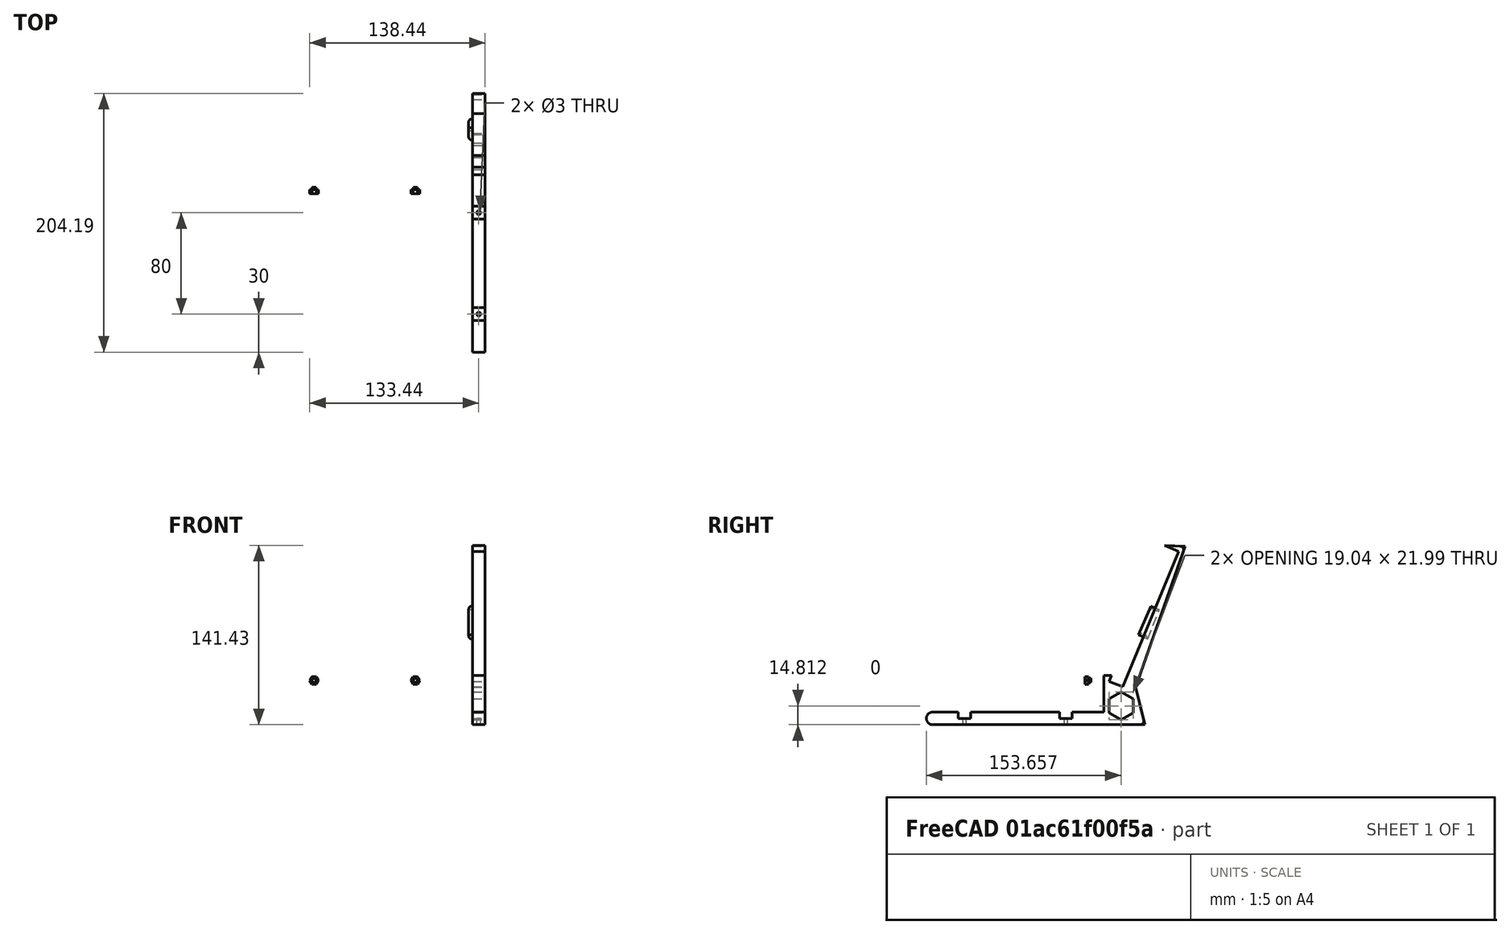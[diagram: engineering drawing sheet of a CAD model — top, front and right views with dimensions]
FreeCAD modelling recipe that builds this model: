
FCSTD DOCUMENT  (FreeCAD 0.16R6704 (Git))
Label: SOPORTE_LATERAL
License: All rights reserved
LicenseURL: http://en.wikipedia.org/wiki/All_rights_reserved
objects: Sketcher::SketchObject×4, PartDesign::Fillet×3, Mesh::Feature×2, PartDesign::Pad×2, PartDesign::Pocket×2
note: 15 computed .brp shape members not serialized (recipe doc carries the construction recipe); baked Part::Feature solids carry a one-line shape summary decoded from their .brp

FEATURE [Mesh::Feature] surround
  Placement = pos=(0,0,0) rot=(1,0,0;1.18682rad)
FEATURE [Sketcher::SketchObject] Sketch
  Placement = pos=(0,0,0) rot=(0.57735,0.57735,0.57735;2.0944rad)
  sketch-geometry (27):
    g0: LineSegment StartX=33.0856 StartY=111.432 StartZ=0 EndX=44.2008 EndY=106.79 EndZ=0
    g1: LineSegment StartX=44.2008 StartY=106.79 StartZ=0 EndX=0 EndY=0 EndZ=0
    g2: LineSegment StartX=-15 StartY=-20 StartZ=0 EndX=-40 EndY=-20 EndZ=0
    g3: LineSegment StartX=-150 StartY=-30 StartZ=0 EndX=17.4847 EndY=-30 EndZ=0
    g4: LineSegment StartX=17.4847 StartY=-30 StartZ=0 EndX=10 EndY=-0.272781 EndZ=0
    g5: LineSegment StartX=10 StartY=-0.272781 StartZ=0 EndX=49.1867 EndY=110.744 EndZ=0
    g6: LineSegment StartX=49.1867 StartY=110.744 StartZ=0 EndX=33.0856 EndY=111.432 EndZ=0
    g7: LineSegment StartX=0 StartY=0 StartZ=0 EndX=-10.9261 EndY=4.19036 EndZ=0
    g8: LineSegment StartX=-10.9261 StartY=4.19036 StartZ=0 EndX=-9.04306 EndY=8.84724 EndZ=0
    g9: LineSegment StartX=-9.04306 StartY=8.84724 StartZ=0 EndX=-15 EndY=8.84724 EndZ=0
    g10: LineSegment StartX=-15 StartY=8.84724 StartZ=0 EndX=-15 EndY=-20 EndZ=0
    g11: LineSegment StartX=8.17828 StartY=-20.6848 StartZ=0 EndX=8.17828 EndY=-9.6906 EndZ=0
    g12: LineSegment StartX=8.17828 StartY=-9.6906 StartZ=0 EndX=-1.34293 EndY=-4.19353 EndZ=0
    g13: LineSegment StartX=-1.34293 StartY=-4.19353 StartZ=0 EndX=-10.8641 EndY=-9.6906 EndZ=0
    g14: LineSegment StartX=-10.8641 StartY=-9.6906 StartZ=0 EndX=-10.8641 EndY=-20.6848 EndZ=0
    g15: LineSegment StartX=-10.8641 StartY=-20.6848 StartZ=0 EndX=-1.34293 EndY=-26.1818 EndZ=0
    g16: LineSegment StartX=-1.34293 StartY=-26.1818 StartZ=0 EndX=8.17828 EndY=-20.6848 EndZ=0
    g17: Circle [constr] CenterX=-1.34293 CenterY=-15.1877 CenterZ=0 NormalX=0 NormalY=0 NormalZ=1 Radius=10.9941
    g18: LineSegment StartX=-130 StartY=-20 StartZ=0 EndX=-130 EndY=-25 EndZ=0
    g19: LineSegment StartX=-130 StartY=-25 StartZ=0 EndX=-120 EndY=-25 EndZ=0
    g20: LineSegment StartX=-120 StartY=-25 StartZ=0 EndX=-120 EndY=-20 EndZ=0
    g21: LineSegment StartX=-130 StartY=-20 StartZ=0 EndX=-150 EndY=-20 EndZ=0
    g22: LineSegment StartX=-50 StartY=-20 StartZ=0 EndX=-50 EndY=-25 EndZ=0
    g23: LineSegment StartX=-50 StartY=-25 StartZ=0 EndX=-40 EndY=-25 EndZ=0
    g24: LineSegment StartX=-40 StartY=-25 StartZ=0 EndX=-40 EndY=-20 EndZ=0
    g25: LineSegment StartX=-50 StartY=-20 StartZ=0 EndX=-120 EndY=-20 EndZ=0
    g26: ArcOfCircle CenterX=-150 CenterY=-25 CenterZ=0 NormalX=0 NormalY=0 NormalZ=1 Radius=5 StartAngle=1.5708 EndAngle=4.71239
  constraints (57):
    c: Coincident(g0,g1)
    c: Coincident(g1,g-1)
    c: Horizontal(g2)
    c: Coincident(g3,g4)
    c: Coincident(g4,g5)
    c: Coincident(g5,g6)
    c: Coincident(g6,g0)
    c: Horizontal(g3)
    c: Coincident(g7,g8)
    c: Coincident(g8,g9)
    c: Coincident(g9,g10)
    c: Coincident(g-1,g7)
    c: Horizontal(g9)
    c: Coincident(g2,g10)
    c: DistanceY(g2,g-1) = 20
    c: DistanceY(g3,g-1) = 30
    c: DistanceX(g-1,g4) = 10
    c: Vertical(g10)
    c: DistanceX(g21,g2) = 135
    c: Coincident(g11,g12)
    c: Coincident(g12,g13)
    c: Coincident(g13,g14)
    c: Coincident(g14,g15)
    c: Coincident(g15,g16)
    c: Coincident(g16,g11)
    c: Equal(g11, g12-g16) x5
    c: PointOnObject(g11,g17)
    c: PointOnObject(g12,g17)
    c: PointOnObject(g13,g17)
    c: PointOnObject(g14,g17)
    c: PointOnObject(g15,g17)
    c: PointOnObject(g16,g17)
    c: Vertical(g14)
    c: DistanceX(g21,g-1) = 150
    c: Coincident(g18,g19)
    c: Horizontal(g19)
    c: Coincident(g19,g20)
    c: Vertical(g20)
    c: Vertical(g18)
    c: DistanceX(g19,g19) = 10
    c: Coincident(g25,g20)
    c: Coincident(g21,g18)
    c: Tangent(g2,g21)
    c: Coincident(g22,g23)
    c: Horizontal(g23)
    c: Coincident(g23,g24)
    c: Vertical(g24)
    c: Vertical(g22)
    c: DistanceX(g23,g23) = 10
    c: DistanceX(g19,g22) = 70
    c: Coincident(g2,g24)
    c: Coincident(g25,g22)
    c: Tangent(g2,g25)
    c: DistanceY(g24,g24) = 5
    c: DistanceY(g20,g20) = 5
    c: Tangent(g26,g21)
    c: Tangent(g3,g26)
FEATURE [PartDesign::Pad] Pad
  Length = 10
  Length2 = 100
  Placement = pos=(0,0,0) rot=(0.57735,0.57735,0.57735;2.0944rad)
  Sketch = -> Sketch
  Type = 0
FEATURE [Sketcher::SketchObject] Sketch001
  ExternalGeometry = -> [Pad]
  Placement = pos=(0,0,-25) rot=(0,0,-1;1.5708rad)
  Support = -> Pad [Face15]
  sketch-geometry (2):
    g0: Circle CenterX=45 CenterY=5 CenterZ=0 NormalX=0 NormalY=0 NormalZ=1 Radius=1.5
    g1: Circle CenterX=125 CenterY=5 CenterZ=0 NormalX=0 NormalY=0 NormalZ=1 Radius=1.5
  constraints (6):
    c: Radius(g0) = 1.5
    c: DistanceY(g-3,g0) = 5
    c: DistanceX(g-3,g0) = 5
    c: Radius(g1) = 1.5
    c: DistanceX(g1,g-4) = 5
    c: DistanceY(g-4,g1) = 5
FEATURE [PartDesign::Pocket] Pocket
  Length = 5
  Placement = pos=(0,0,0) rot=(0.57735,0.57735,0.57735;2.0944rad)
  Sketch = -> Sketch001
  Type = 0
FEATURE [Sketcher::SketchObject] Sketch003
  ExternalGeometry = -> [Pocket]
  Placement = pos=(0,0,0) rot=(0.57735,0.57735,-0.57735;4.18879rad)
  Support = -> Pocket [Face4]
  sketch-geometry (4):
    g0: LineSegment StartX=19.5719 StartY=-37.6948 StartZ=0 EndX=28.8724 EndY=-60.696 EndZ=0
    g1: LineSegment StartX=28.8724 StartY=-60.696 StartZ=0 EndX=22.072 EndY=-63.3961 EndZ=0
    g2: LineSegment StartX=22.072 StartY=-63.3961 StartZ=0 EndX=12.4716 EndY=-40.895 EndZ=0
    g3: LineSegment StartX=12.4716 StartY=-40.895 StartZ=0 EndX=19.5719 EndY=-37.6948 EndZ=0
  constraints (4):
    c: Coincident(g0,g1)
    c: Coincident(g1,g2)
    c: Coincident(g2,g3)
    c: Coincident(g3,g0)
FEATURE [PartDesign::Pad] Pad001
  Length = 3
  Length2 = 100
  Placement = pos=(0,0,0) rot=(0.57735,0.57735,0.57735;2.0944rad)
  Sketch = -> Sketch003
  Type = 0
FEATURE [PartDesign::Fillet] Fillet
  Base = -> Pad001 [Edge77,Edge73,Edge100,Edge80]
  Placement = pos=(0,0,0) rot=(0.57735,0.57735,0.57735;2.0944rad)
  Radius = 2
FEATURE [PartDesign::Fillet] Fillet001
  Base = -> Fillet [Edge62]
  Placement = pos=(0,0,0) rot=(0.57735,0.57735,0.57735;2.0944rad)
  Radius = 3
FEATURE [PartDesign::Fillet] Fillet002
  Base = -> Fillet001 [Edge37]
  Placement = pos=(0,0,0) rot=(0.57735,0.57735,0.57735;2.0944rad)
  Radius = 3
FEATURE [Sketcher::SketchObject] Sketch002
  Placement = pos=(0,0,-30) rot=(0.707107,0.707107,0;3.14159rad)
  Support = -> Fillet002 [Face5]
  sketch-geometry (14):
    g0: LineSegment StartX=-123.239 StartY=1.96418 StartZ=0 EndX=-121.507 EndY=4.96418 EndZ=0
    g1: LineSegment StartX=-121.507 StartY=4.96418 StartZ=0 EndX=-123.239 EndY=7.96418 EndZ=0
    g2: LineSegment StartX=-123.239 StartY=7.96418 StartZ=0 EndX=-126.704 EndY=7.96418 EndZ=0
    g3: LineSegment StartX=-126.704 StartY=7.96418 StartZ=0 EndX=-128.436 EndY=4.96418 EndZ=0
    g4: LineSegment StartX=-128.436 StartY=4.96418 StartZ=0 EndX=-126.704 EndY=1.96418 EndZ=0
    g5: LineSegment StartX=-126.704 StartY=1.96418 StartZ=0 EndX=-123.239 EndY=1.96418 EndZ=0
    g6: Circle [constr] CenterX=-124.971 CenterY=4.96418 CenterZ=0 NormalX=0 NormalY=0 NormalZ=1 Radius=3.4641
    g7: LineSegment StartX=-43.3346 StartY=7.98064 StartZ=0 EndX=-46.7987 EndY=7.98064 EndZ=0
    g8: LineSegment StartX=-46.7987 StartY=7.98064 StartZ=0 EndX=-48.5308 EndY=4.98064 EndZ=0
    g9: LineSegment StartX=-48.5308 StartY=4.98064 StartZ=0 EndX=-46.7987 EndY=1.98064 EndZ=0
    g10: LineSegment StartX=-46.7987 StartY=1.98064 StartZ=0 EndX=-43.3346 EndY=1.98064 EndZ=0
    g11: LineSegment StartX=-43.3346 StartY=1.98064 StartZ=0 EndX=-41.6026 EndY=4.98064 EndZ=0
    g12: LineSegment StartX=-41.6026 StartY=4.98064 StartZ=0 EndX=-43.3346 EndY=7.98064 EndZ=0
    g13: Circle [constr] CenterX=-45.0667 CenterY=4.98064 CenterZ=0 NormalX=0 NormalY=0 NormalZ=1 Radius=3.4641
  constraints (30):
    c: Coincident(g0,g1)
    c: Coincident(g1,g2)
    c: Coincident(g2,g3)
    c: Coincident(g3,g4)
    c: Coincident(g4,g5)
    c: Coincident(g5,g0)
    c: Equal(g0, g1-g5) x5
    c: PointOnObject(g0,g6)
    c: PointOnObject(g1,g6)
    c: PointOnObject(g2,g6)
    c: PointOnObject(g3,g6)
    c: PointOnObject(g4,g6)
    c: PointOnObject(g5,g6)
    c: Horizontal(g2)
    c: DistanceY(g0,g1) = 6
    c: Coincident(g7,g8)
    c: Coincident(g8,g9)
    c: Coincident(g9,g10)
    c: Coincident(g10,g11)
    c: Coincident(g11,g12)
    c: Coincident(g12,g7)
    c: Equal(g7, g8-g12) x5
    c: PointOnObject(g7,g13)
    c: PointOnObject(g8,g13)
    c: PointOnObject(g9,g13)
    c: PointOnObject(g10,g13)
    c: PointOnObject(g11,g13)
    c: PointOnObject(g12,g13)
    c: Horizontal(g7)
    c: DistanceY(g10,g7) = 6
FEATURE [PartDesign::Pocket] Pocket001
  Length = 3
  Placement = pos=(0,0,0) rot=(0.57735,0.57735,0.57735;2.0944rad)
  Sketch = -> Sketch002
  Type = 0
FEATURE [Mesh::Feature] SOPORTE_LATERAL_LADO
  Placement = pos=(189.5,0,0) rot=(0,0,1;0rad)
